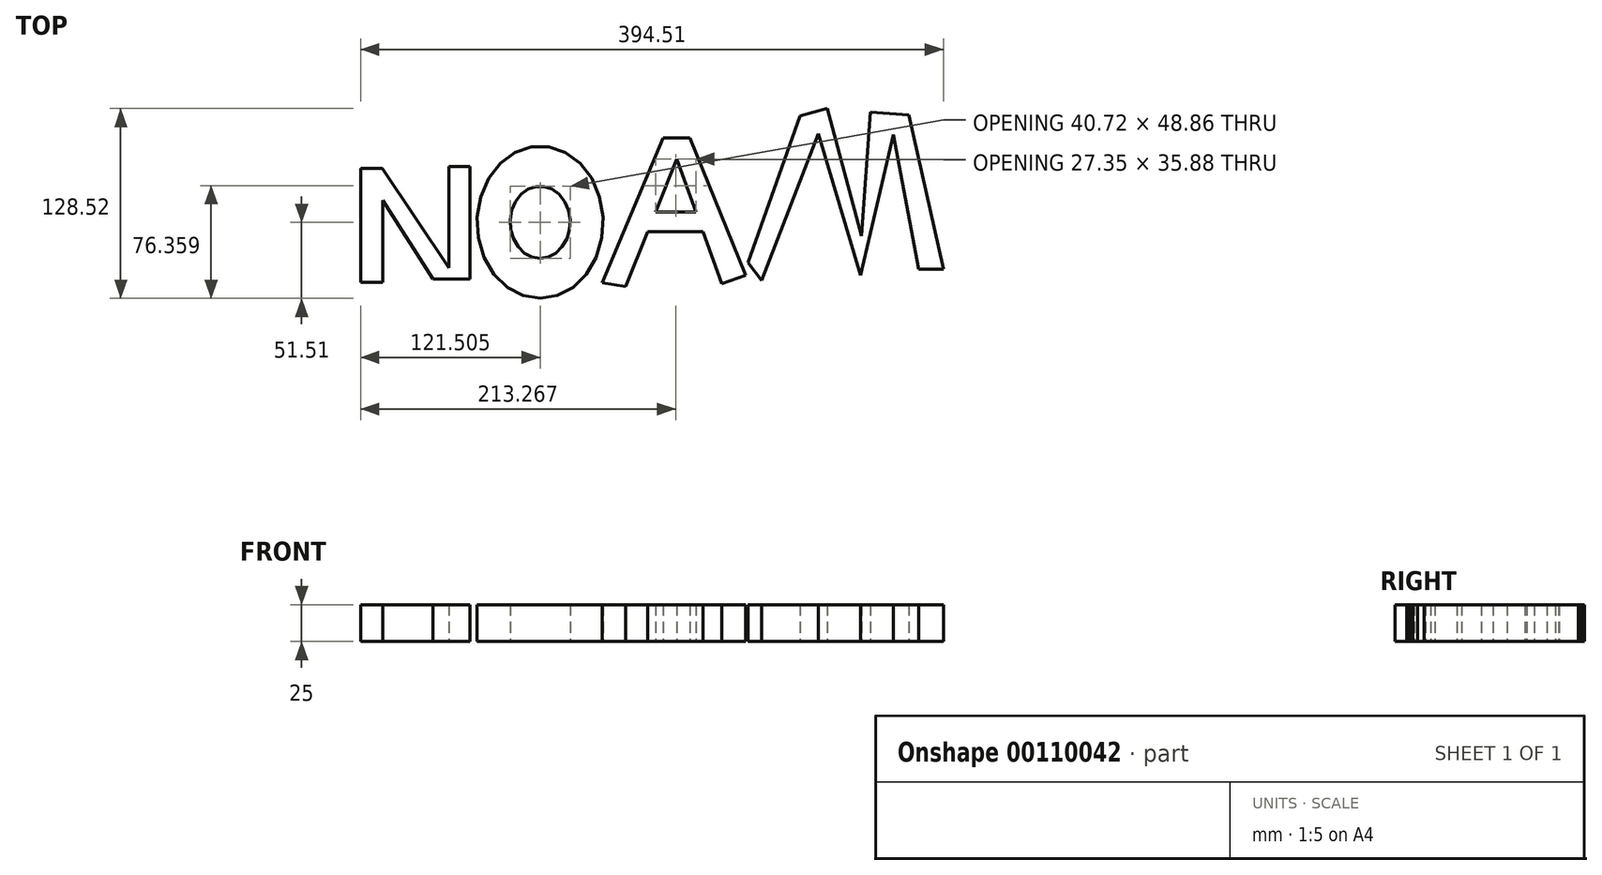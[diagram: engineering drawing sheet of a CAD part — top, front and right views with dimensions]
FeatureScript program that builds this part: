
annotation { "Feature Type Name" : "Feature", "Feature Type Description" : "" }
export const myFeature = defineFeature(function(context is Context, id is Id, definition is map)
    precondition{}
    {
        {
            var Q0;
            Q0=qCreatedBy(makeId("Top.planeOp"),FACE);
            var sketch = newSketch(context, id + "F0", { "sketchPlane" : qUnion([Q0])});
            skEllipse(sketch, "E0", {"center": v(-29.43, -12.25) * mm, "majorRadius": 51.5 * mm, "minorRadius": 42.72 * mm, "majorAxis": v(0, -1)});
            skLineSegment(sketch, "E1", {"start": v(-136.46, 24.2) * mm, "end": v(-150.94, 24.2) * mm});
            skLineSegment(sketch, "E2", {"start": v(-136.46, 24.2) * mm, "end": v(-91.22, -42.97) * mm});
            skLineSegment(sketch, "E3", {"start": v(-91.22, -42.97) * mm, "end": v(-91.22, 25.56) * mm});
            skLineSegment(sketch, "E4", {"start": v(-91.22, 25.56) * mm, "end": v(-77.04, 25.56) * mm});
            skLineSegment(sketch, "E5", {"start": v(-77.04, 25.56) * mm, "end": v(-77.04, -50.74) * mm});
            skLineSegment(sketch, "E6", {"start": v(-77.04, -50.74) * mm, "end": v(-101.94, -50.74) * mm});
            skLineSegment(sketch, "E7", {"start": v(-135.92, 2.68) * mm, "end": v(-101.94, -50.74) * mm});
            skLineSegment(sketch, "E8", {"start": v(-150.94, 24.2) * mm, "end": v(-150.94, -52.76) * mm});
            skLineSegment(sketch, "E9", {"start": v(-135.92, 2.68) * mm, "end": v(-135.92, -52.76) * mm});
            skLineSegment(sketch, "E10", {"start": v(-150.94, -52.76) * mm, "end": v(-135.92, -52.76) * mm});
            skLineSegment(sketch, "E11", {"start": v(62.97, 30.54) * mm, "end": v(28.49, -55.86) * mm});
            skLineSegment(sketch, "E12", {"start": v(62.97, 30.54) * mm, "end": v(93.67, -53.97) * mm});
            skLineSegment(sketch, "E13", {"start": v(43.33, -18.68) * mm, "end": v(80.85, -18.68) * mm});
            skLineSegment(sketch, "E14", {"start": v(48.65, -5.34) * mm, "end": v(76, -5.34) * mm});
            skLineSegment(sketch, "E15", {"start": v(93.67, -53.97) * mm, "end": v(109.67, -48.15) * mm});
            skLineSegment(sketch, "E16", {"start": v(12.57, -53.2) * mm, "end": v(29.62, -55.86) * mm});
            skLineSegment(sketch, "E17", {"start": v(109.67, -48.15) * mm, "end": v(72.07, 44.94) * mm});
            skLineSegment(sketch, "E18", {"start": v(72.07, 44.94) * mm, "end": v(53.88, 44.94) * mm});
            skLineSegment(sketch, "E19", {"start": v(53.88, 44.94) * mm, "end": v(12.57, -53.2) * mm});
            skLineSegment(sketch, "E20", {"start": v(120.57, -51.7) * mm, "end": v(158.85, 47.6) * mm});
            skLineSegment(sketch, "E21", {"start": v(158.85, 47.6) * mm, "end": v(187.65, -48.28) * mm});
            skLineSegment(sketch, "E22", {"start": v(187.65, -48.28) * mm, "end": v(209.63, 47.21) * mm});
            skLineSegment(sketch, "E23", {"start": v(209.63, 47.21) * mm, "end": v(226.77, -43.89) * mm});
            skLineSegment(sketch, "E24", {"start": v(226.77, -43.89) * mm, "end": v(243.57, -43.89) * mm});
            skLineSegment(sketch, "E25", {"start": v(243.57, -43.89) * mm, "end": v(220.3, 60.39) * mm});
            skLineSegment(sketch, "E26", {"start": v(220.3, 60.39) * mm, "end": v(194.25, 62.28) * mm});
            skLineSegment(sketch, "E27", {"start": v(194.25, 62.28) * mm, "end": v(188.14, -21.62) * mm});
            skLineSegment(sketch, "E28", {"start": v(188.14, -21.62) * mm, "end": v(165.13, 64.76) * mm});
            skLineSegment(sketch, "E29", {"start": v(165.13, 64.76) * mm, "end": v(146.51, 59.8) * mm});
            skLineSegment(sketch, "E30", {"start": v(146.51, 59.8) * mm, "end": v(111.37, -39.43) * mm});
            skLineSegment(sketch, "E31", {"start": v(111.37, -39.43) * mm, "end": v(120.57, -51.7) * mm});
            skEllipse(sketch, "E32", {"center": v(-29.43, -12.25) * mm, "majorRadius": 24.43 * mm, "minorRadius": 20.36 * mm, "majorAxis": v(0, -1)});
            skSolve(sketch);
        }
        {
            var Q0;
            Q0 = qSketchRegion(id + "F0", true);
            extrude(context, id + "F1", {"entities" : qUnion([Q0]), "depth" : 25 * mm});
        }
    });
